SOLIDWORKS PART (.sldprt)
format: sldprt  version: not decoded by parser v0  size: 116,736 bytes
history: native  units: mm
features: plane x3, sketch x3, cut_extrude x2, material x1, extrude x1, fillet x1, mirror x1 (+13 scaffold rows collapsed)
feature tree (25):
  scaffold x13  (default folders/planes/origin — collapsed)
  material  "Material <nicht festgelegt>"
  plane  "Ebene vorne"
  plane  "Ebene oben"
  plane  "Ebene rechts"
  sketch  "Skizze1"  dims[D1=75.0mm]
  extrude  "Linear austragen1"  Depth=10mm
  sketch  "Skizze2"  dims[D1=10.0mm D2=100.0mm D3=60.0mm]
  cut_extrude  "Schnitt-Linear austragen1"  Depth=10mm
  fillet  "Verrundung1"  Radius=3mm
  sketch  "Skizze4"  dims[D1=30.0mm]
  cut_extrude  "Schnitt-Linear austragen2"  Depth=30mm
  mirror  "Spiegeln1"
decode coverage: 7 of 8 modeling features carry decoded parameters
note: suppression state not decoded; provenance and decode notes live in map.json
